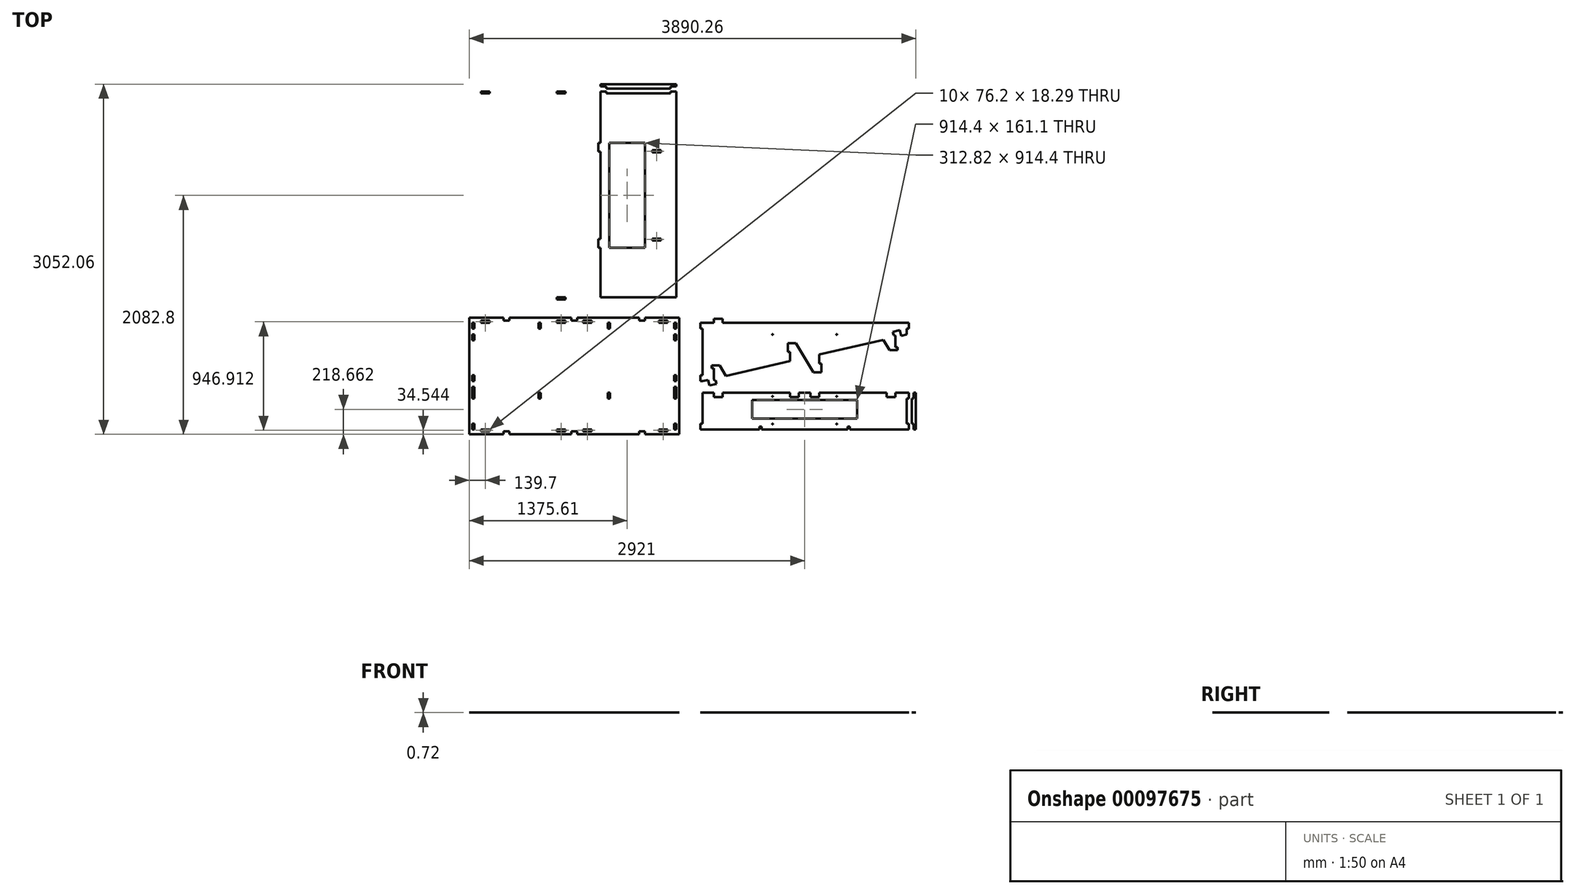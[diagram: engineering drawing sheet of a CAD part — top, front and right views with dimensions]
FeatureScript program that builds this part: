
annotation { "Feature Type Name" : "Feature", "Feature Type Description" : "" }
export const myFeature = defineFeature(function(context is Context, id is Id, definition is map)
    precondition{}
    {
        {
            assignVariable(context, id + "F0", {"name" : "ply34", "anyValue" : .72});
        }
        {
            var Q0;
            Q0=qCreatedBy(makeId("Top.planeOp"),FACE);
            var sketch = newSketch(context, id + "F1", { "sketchPlane" : qUnion([Q0])});
            skLineSegment(sketch, "E0.bottom", {"start": v(914.4, 508) * mm, "end": v(-914.4, 508) * mm});
            skLineSegment(sketch, "E0.top", {"start": v(914.4, -508) * mm, "end": v(-914.4, -508) * mm});
            skLineSegment(sketch, "E0.left", {"start": v(914.4, 508) * mm, "end": v(914.4, -508) * mm});
            skLineSegment(sketch, "E0.right", {"start": v(-914.4, 508) * mm, "end": v(-914.4, -508) * mm});
            skPoint(sketch, "E0.middle", {"position": v(0, 0) * mm});
            skLineSegment(sketch, "E1.bottom", {"start": v(889, 482.6) * mm, "end": v(-889, 482.6) * mm, "construction": true});
            skLineSegment(sketch, "E1.top", {"start": v(889, -482.6) * mm, "end": v(-889, -482.6) * mm, "construction": true});
            skLineSegment(sketch, "E1.left", {"start": v(889, 482.6) * mm, "end": v(889, -482.6) * mm, "construction": true});
            skLineSegment(sketch, "E1.right", {"start": v(-889, 482.6) * mm, "end": v(-889, -482.6) * mm, "construction": true});
            skLineSegment(sketch, "E2", {"start": v(0, 482.6) * mm, "end": v(0, -482.6) * mm, "construction": true});
            skLineSegment(sketch, "E3", {"start": v(0, 0) * mm, "end": v(-889, 0) * mm, "construction": true});
            skLineSegment(sketch, "E4", {"start": v(-444.5, 482.6) * mm, "end": v(-444.5, -482.6) * mm, "construction": true});
            skPoint(sketch, "E4.startSnap0", {"position": v(-444.5, 0) * mm});
            skLineSegment(sketch, "E5.bottom", {"start": v(-812.8, 482.6) * mm, "end": v(-736.6, 482.6) * mm});
            skLineSegment(sketch, "E5.top", {"start": v(-812.8, 464.31) * mm, "end": v(-736.6, 464.31) * mm});
            skLineSegment(sketch, "E5.left", {"start": v(-812.8, 482.6) * mm, "end": v(-812.8, 464.31) * mm});
            skLineSegment(sketch, "E5.right", {"start": v(-736.6, 482.6) * mm, "end": v(-736.6, 464.31) * mm});
            skLineSegment(sketch, "E6.MirrorCS", {"start": v(-76.2, 482.6) * mm, "end": v(-152.4, 482.6) * mm});
            skLineSegment(sketch, "E7.MirrorCS", {"start": v(-76.2, 464.31) * mm, "end": v(-152.4, 464.31) * mm});
            skLineSegment(sketch, "E8.MirrorCS", {"start": v(-152.4, 482.6) * mm, "end": v(-152.4, 464.31) * mm});
            skLineSegment(sketch, "E9.MirrorCS", {"start": v(-76.2, 482.6) * mm, "end": v(-76.2, 464.31) * mm});
            skLineSegment(sketch, "E10.MirrorCS", {"start": v(76.2, 482.6) * mm, "end": v(76.2, 464.31) * mm});
            skLineSegment(sketch, "E11.MirrorCS", {"start": v(736.6, 482.6) * mm, "end": v(736.6, 464.31) * mm});
            skLineSegment(sketch, "E12.MirrorCS", {"start": v(152.4, 482.6) * mm, "end": v(152.4, 464.31) * mm});
            skLineSegment(sketch, "E13.MirrorCS", {"start": v(812.8, 482.6) * mm, "end": v(812.8, 464.31) * mm});
            skLineSegment(sketch, "E14.MirrorCS", {"start": v(812.8, 482.6) * mm, "end": v(736.6, 482.6) * mm});
            skLineSegment(sketch, "E15.MirrorCS", {"start": v(76.2, 482.6) * mm, "end": v(152.4, 482.6) * mm});
            skLineSegment(sketch, "E16.MirrorCS", {"start": v(812.8, 464.31) * mm, "end": v(736.6, 464.31) * mm});
            skLineSegment(sketch, "E17.MirrorCS", {"start": v(76.2, 464.31) * mm, "end": v(152.4, 464.31) * mm});
            skLineSegment(sketch, "E18.MirrorCS", {"start": v(812.8, -482.6) * mm, "end": v(812.8, -464.31) * mm});
            skLineSegment(sketch, "E19.MirrorCS", {"start": v(-76.2, -482.6) * mm, "end": v(-76.2, -464.31) * mm});
            skLineSegment(sketch, "E20.MirrorCS", {"start": v(736.6, -482.6) * mm, "end": v(736.6, -464.31) * mm});
            skLineSegment(sketch, "E21.MirrorCS", {"start": v(-152.4, -482.6) * mm, "end": v(-152.4, -464.31) * mm});
            skLineSegment(sketch, "E22.MirrorCS", {"start": v(152.4, -482.6) * mm, "end": v(152.4, -464.31) * mm});
            skLineSegment(sketch, "E23.MirrorCS", {"start": v(-812.8, -482.6) * mm, "end": v(-812.8, -464.31) * mm});
            skLineSegment(sketch, "E24.MirrorCS", {"start": v(76.2, -482.6) * mm, "end": v(76.2, -464.31) * mm});
            skLineSegment(sketch, "E25.MirrorCS", {"start": v(-736.6, -482.6) * mm, "end": v(-736.6, -464.31) * mm});
            skLineSegment(sketch, "E26.MirrorCS", {"start": v(76.2, -482.6) * mm, "end": v(152.4, -482.6) * mm});
            skLineSegment(sketch, "E27.MirrorCS", {"start": v(812.8, -464.31) * mm, "end": v(736.6, -464.31) * mm});
            skLineSegment(sketch, "E28.MirrorCS", {"start": v(812.8, -482.6) * mm, "end": v(736.6, -482.6) * mm});
            skLineSegment(sketch, "E29.MirrorCS", {"start": v(-76.2, -464.31) * mm, "end": v(-152.4, -464.31) * mm});
            skLineSegment(sketch, "E30.MirrorCS", {"start": v(-76.2, -482.6) * mm, "end": v(-152.4, -482.6) * mm});
            skLineSegment(sketch, "E31.MirrorCS", {"start": v(76.2, -464.31) * mm, "end": v(152.4, -464.31) * mm});
            skLineSegment(sketch, "E32.MirrorCS", {"start": v(-812.8, -464.31) * mm, "end": v(-736.6, -464.31) * mm});
            skLineSegment(sketch, "E33.MirrorCS", {"start": v(-812.8, -482.6) * mm, "end": v(-736.6, -482.6) * mm});
            skLineSegment(sketch, "E34.bottom", {"start": v(292.1, 464.31) * mm, "end": v(310.39, 464.31) * mm});
            skLineSegment(sketch, "E34.top", {"start": v(292.1, 413.51) * mm, "end": v(310.39, 413.51) * mm});
            skLineSegment(sketch, "E34.left", {"start": v(292.1, 464.31) * mm, "end": v(292.1, 413.51) * mm});
            skLineSegment(sketch, "E34.right", {"start": v(310.39, 464.31) * mm, "end": v(310.39, 413.51) * mm});
            skLineSegment(sketch, "E35.bottom", {"start": v(292.1, -145.29) * mm, "end": v(310.39, -145.29) * mm});
            skLineSegment(sketch, "E35.top", {"start": v(292.1, -196.09) * mm, "end": v(310.39, -196.09) * mm});
            skLineSegment(sketch, "E35.left", {"start": v(292.1, -145.29) * mm, "end": v(292.1, -196.09) * mm});
            skLineSegment(sketch, "E35.right", {"start": v(310.39, -145.29) * mm, "end": v(310.39, -196.09) * mm});
            skLineSegment(sketch, "E36.MirrorCS", {"start": v(-292.1, -196.09) * mm, "end": v(-310.39, -196.09) * mm});
            skLineSegment(sketch, "E37.MirrorCS", {"start": v(-292.1, -145.29) * mm, "end": v(-310.39, -145.29) * mm});
            skLineSegment(sketch, "E38.MirrorCS", {"start": v(-292.1, 413.51) * mm, "end": v(-310.39, 413.51) * mm});
            skLineSegment(sketch, "E39.MirrorCS", {"start": v(-292.1, 464.31) * mm, "end": v(-310.39, 464.31) * mm});
            skLineSegment(sketch, "E40.MirrorCS", {"start": v(-292.1, -145.29) * mm, "end": v(-292.1, -196.09) * mm});
            skLineSegment(sketch, "E41.MirrorCS", {"start": v(-310.39, 464.31) * mm, "end": v(-310.39, 413.51) * mm});
            skLineSegment(sketch, "E42.MirrorCS", {"start": v(-310.39, -145.29) * mm, "end": v(-310.39, -196.09) * mm});
            skLineSegment(sketch, "E43.MirrorCS", {"start": v(-292.1, 464.31) * mm, "end": v(-292.1, 413.51) * mm});
            skLineSegment(sketch, "E44.bottom", {"start": v(-889, 685.8) * mm, "end": v(0, 685.8) * mm});
            skLineSegment(sketch, "E44.top", {"start": v(-889, 2463.8) * mm, "end": v(0, 2463.8) * mm});
            skLineSegment(sketch, "E44.left", {"start": v(-889, 685.8) * mm, "end": v(-889, 2463.8) * mm});
            skLineSegment(sketch, "E44.right", {"start": v(0, 685.8) * mm, "end": v(0, 2463.8) * mm});
            skLineSegment(sketch, "E45.bottom", {"start": v(-812.8, 685.8) * mm, "end": v(-736.6, 685.8) * mm});
            skLineSegment(sketch, "E45.top", {"start": v(-812.8, 667.51) * mm, "end": v(-736.6, 667.51) * mm});
            skLineSegment(sketch, "E45.left", {"start": v(-812.8, 685.8) * mm, "end": v(-812.8, 667.51) * mm});
            skLineSegment(sketch, "E45.right", {"start": v(-736.6, 685.8) * mm, "end": v(-736.6, 667.51) * mm});
            skLineSegment(sketch, "E46", {"start": v(-444.5, 685.8) * mm, "end": v(-444.5, 2463.8) * mm, "construction": true});
            skLineSegment(sketch, "E47", {"start": v(0, 1574.8) * mm, "end": v(-889, 1574.8) * mm, "construction": true});
            skLineSegment(sketch, "E48.MirrorCS", {"start": v(-76.2, 667.51) * mm, "end": v(-152.4, 667.51) * mm});
            skLineSegment(sketch, "E49.MirrorCS", {"start": v(-76.2, 685.8) * mm, "end": v(-152.4, 685.8) * mm});
            skLineSegment(sketch, "E50.MirrorCS", {"start": v(-152.4, 685.8) * mm, "end": v(-152.4, 667.51) * mm});
            skLineSegment(sketch, "E51.MirrorCS", {"start": v(-76.2, 685.8) * mm, "end": v(-76.2, 667.51) * mm});
            skLineSegment(sketch, "E52.MirrorCS", {"start": v(-812.8, 2482.09) * mm, "end": v(-736.6, 2482.09) * mm});
            skLineSegment(sketch, "E53.MirrorCS", {"start": v(-812.8, 2463.8) * mm, "end": v(-736.6, 2463.8) * mm});
            skLineSegment(sketch, "E54.MirrorCS", {"start": v(-812.8, 2463.8) * mm, "end": v(-812.8, 2482.09) * mm});
            skLineSegment(sketch, "E55.MirrorCS", {"start": v(-736.6, 2463.8) * mm, "end": v(-736.6, 2482.09) * mm});
            skLineSegment(sketch, "E56.MirrorCS", {"start": v(-152.4, 2463.8) * mm, "end": v(-152.4, 2482.09) * mm});
            skLineSegment(sketch, "E57.MirrorCS", {"start": v(-76.2, 2463.8) * mm, "end": v(-76.2, 2482.09) * mm});
            skLineSegment(sketch, "E58.MirrorCS", {"start": v(-76.2, 2482.09) * mm, "end": v(-152.4, 2482.09) * mm});
            skLineSegment(sketch, "E59.MirrorCS", {"start": v(-76.2, 2463.8) * mm, "end": v(-152.4, 2463.8) * mm});
            skLineSegment(sketch, "E60.0", {"start": v(870.71, 464.31) * mm, "end": v(-870.71, 464.31) * mm, "construction": true});
            skLineSegment(sketch, "E60.1", {"start": v(870.71, 464.31) * mm, "end": v(870.71, -464.31) * mm, "construction": true});
            skLineSegment(sketch, "E60.2", {"start": v(870.71, -464.31) * mm, "end": v(-870.71, -464.31) * mm, "construction": true});
            skLineSegment(sketch, "E60.3", {"start": v(-870.71, 464.31) * mm, "end": v(-870.71, -464.31) * mm, "construction": true});
            skLineSegment(sketch, "E61.bottom", {"start": v(-310.39, 464.31) * mm, "end": v(-292.1, 464.31) * mm, "construction": true});
            skLineSegment(sketch, "E61.top", {"start": v(-310.39, -196.09) * mm, "end": v(-292.1, -196.09) * mm, "construction": true});
            skLineSegment(sketch, "E61.left", {"start": v(-310.39, 464.31) * mm, "end": v(-310.39, -196.09) * mm, "construction": true});
            skLineSegment(sketch, "E61.right", {"start": v(-292.1, 464.31) * mm, "end": v(-292.1, -196.09) * mm, "construction": true});
            skLineSegment(sketch, "E62.bottom", {"start": v(292.1, 464.31) * mm, "end": v(310.39, 464.31) * mm, "construction": true});
            skLineSegment(sketch, "E62.top", {"start": v(292.1, -196.09) * mm, "end": v(310.39, -196.09) * mm, "construction": true});
            skLineSegment(sketch, "E62.left", {"start": v(292.1, 464.31) * mm, "end": v(292.1, -196.09) * mm, "construction": true});
            skLineSegment(sketch, "E62.right", {"start": v(310.39, 464.31) * mm, "end": v(310.39, -196.09) * mm, "construction": true});
            skLineSegment(sketch, "E63.bottom", {"start": v(228.6, 685.8) * mm, "end": v(889, 685.8) * mm});
            skLineSegment(sketch, "E63.top", {"start": v(228.6, 2463.8) * mm, "end": v(889, 2463.8) * mm});
            skLineSegment(sketch, "E63.left", {"start": v(228.6, 685.8) * mm, "end": v(228.6, 2463.8) * mm});
            skLineSegment(sketch, "E63.right", {"start": v(889, 685.8) * mm, "end": v(889, 2463.8) * mm});
            skLineSegment(sketch, "E64.bottom", {"start": v(228.6, 685.8) * mm, "end": v(279.4, 685.8) * mm});
            skLineSegment(sketch, "E64.top", {"start": v(228.6, 667.51) * mm, "end": v(279.4, 667.51) * mm});
            skLineSegment(sketch, "E64.left", {"start": v(228.6, 685.8) * mm, "end": v(228.6, 667.51) * mm});
            skLineSegment(sketch, "E64.right", {"start": v(279.4, 685.8) * mm, "end": v(279.4, 667.51) * mm});
            skLineSegment(sketch, "E65", {"start": v(558.8, 685.8) * mm, "end": v(558.8, 2463.8) * mm, "construction": true});
            skLineSegment(sketch, "E66", {"start": v(889, 1574.8) * mm, "end": v(228.6, 1574.8) * mm, "construction": true});
            skLineSegment(sketch, "E67.MirrorCS", {"start": v(889, 685.8) * mm, "end": v(838.2, 685.8) * mm});
            skLineSegment(sketch, "E68.MirrorCS", {"start": v(838.2, 685.8) * mm, "end": v(838.2, 667.51) * mm});
            skLineSegment(sketch, "E69.MirrorCS", {"start": v(889, 667.51) * mm, "end": v(838.2, 667.51) * mm});
            skLineSegment(sketch, "E70.MirrorCS", {"start": v(889, 685.8) * mm, "end": v(889, 667.51) * mm});
            skLineSegment(sketch, "E71.MirrorCS", {"start": v(889, 2463.8) * mm, "end": v(889, 2482.09) * mm});
            skLineSegment(sketch, "E72.MirrorCS", {"start": v(889, 2482.09) * mm, "end": v(838.2, 2482.09) * mm});
            skLineSegment(sketch, "E73.MirrorCS", {"start": v(838.2, 2463.8) * mm, "end": v(838.2, 2482.09) * mm});
            skLineSegment(sketch, "E74.MirrorCS", {"start": v(889, 2463.8) * mm, "end": v(838.2, 2463.8) * mm});
            skLineSegment(sketch, "E75.MirrorCS", {"start": v(228.6, 2463.8) * mm, "end": v(228.6, 2482.09) * mm});
            skLineSegment(sketch, "E76.MirrorCS", {"start": v(228.6, 2463.8) * mm, "end": v(279.4, 2463.8) * mm});
            skLineSegment(sketch, "E77.MirrorCS", {"start": v(279.4, 2463.8) * mm, "end": v(279.4, 2482.09) * mm});
            skLineSegment(sketch, "E78.MirrorCS", {"start": v(228.6, 2482.09) * mm, "end": v(279.4, 2482.09) * mm});
            skPoint(sketch, "E79.middle", {"position": v(558.8, 1574.8) * mm});
            skLineSegment(sketch, "E80.bottom", {"start": v(304.8, 2032) * mm, "end": v(617.62, 2032) * mm});
            skLineSegment(sketch, "E80.top", {"start": v(304.8, 1117.6) * mm, "end": v(617.62, 1117.6) * mm});
            skLineSegment(sketch, "E80.left", {"start": v(304.8, 2032) * mm, "end": v(304.8, 1117.6) * mm});
            skLineSegment(sketch, "E80.right", {"start": v(617.62, 2032) * mm, "end": v(617.62, 1117.6) * mm});
            skLineSegment(sketch, "E81", {"start": v(304.8, 1574.8) * mm, "end": v(617.62, 1574.8) * mm});
            skLineSegment(sketch, "E82.bottom", {"start": v(1117.6, 464.31) * mm, "end": v(2895.6, 464.31) * mm, "construction": true});
            skLineSegment(sketch, "E82.top", {"start": v(1117.6, -145.29) * mm, "end": v(2895.6, -145.29) * mm, "construction": true});
            skLineSegment(sketch, "E82.left", {"start": v(1117.6, 464.31) * mm, "end": v(1117.6, -145.29) * mm, "construction": true});
            skLineSegment(sketch, "E82.right", {"start": v(2895.6, 464.31) * mm, "end": v(2895.6, -145.29) * mm, "construction": true});
            skLineSegment(sketch, "E83", {"start": v(2133.6, 464.31) * mm, "end": v(2133.6, -145.29) * mm, "construction": true});
            skLineSegment(sketch, "E84", {"start": v(1117.6, -43.69) * mm, "end": v(2895.6, -43.69) * mm, "construction": true});
            skLineSegment(sketch, "E85", {"start": v(1117.6, 362.71) * mm, "end": v(2895.6, 362.71) * mm, "construction": true});
            skLineSegment(sketch, "E86", {"start": v(1117.6, 464.31) * mm, "end": v(2895.6, 464.31) * mm});
            skLineSegment(sketch, "E87", {"start": v(2895.6, 464.31) * mm, "end": v(2895.6, 362.71) * mm});
            skLineSegment(sketch, "E88", {"start": v(2895.6, 362.71) * mm, "end": v(1117.6, -43.69) * mm});
            skLineSegment(sketch, "E89", {"start": v(1117.6, -43.69) * mm, "end": v(1117.6, 464.31) * mm});
            skLineSegment(sketch, "E90", {"start": v(2133.6, 188.54) * mm, "end": v(2133.6, 32.51) * mm});
            skLineSegment(sketch, "E91", {"start": v(2133.6, 32.51) * mm, "end": v(2082.8, 32.51) * mm});
            skLineSegment(sketch, "E92", {"start": v(2082.8, 32.51) * mm, "end": v(2006.6, 159.51) * mm});
            skLineSegment(sketch, "E93.bottom", {"start": v(2133.6, 464.31) * mm, "end": v(2057.4, 464.31) * mm});
            skLineSegment(sketch, "E93.top", {"start": v(2133.6, 500.89) * mm, "end": v(2057.4, 500.89) * mm});
            skLineSegment(sketch, "E93.left", {"start": v(2133.6, 464.31) * mm, "end": v(2133.6, 500.89) * mm});
            skLineSegment(sketch, "E93.right", {"start": v(2057.4, 464.31) * mm, "end": v(2057.4, 500.89) * mm});
            skLineSegment(sketch, "E94.bottom", {"start": v(2133.6, 32.51) * mm, "end": v(2151.89, 32.51) * mm});
            skLineSegment(sketch, "E94.top", {"start": v(2133.6, 108.71) * mm, "end": v(2151.89, 108.71) * mm});
            skLineSegment(sketch, "E94.left", {"start": v(2133.6, 32.51) * mm, "end": v(2133.6, 108.71) * mm});
            skLineSegment(sketch, "E94.right", {"start": v(2151.89, 32.51) * mm, "end": v(2151.89, 108.71) * mm});
            skLineSegment(sketch, "E95", {"start": v(1879.6, 464.31) * mm, "end": v(1879.6, -145.29) * mm, "construction": true});
            skLineSegment(sketch, "E96.bottom", {"start": v(1879.6, 286.51) * mm, "end": v(1861.31, 286.51) * mm});
            skLineSegment(sketch, "E96.top", {"start": v(1879.6, 210.31) * mm, "end": v(1861.31, 210.31) * mm});
            skLineSegment(sketch, "E96.left", {"start": v(1879.6, 286.51) * mm, "end": v(1879.6, 210.31) * mm});
            skLineSegment(sketch, "E96.right", {"start": v(1861.31, 286.51) * mm, "end": v(1861.31, 210.31) * mm});
            skLineSegment(sketch, "E97", {"start": v(1879.6, 286.51) * mm, "end": v(1930.4, 286.51) * mm});
            skLineSegment(sketch, "E98", {"start": v(1879.6, 210.31) * mm, "end": v(1879.6, 130.48) * mm});
            skLineSegment(sketch, "E99.bottom", {"start": v(1879.6, -145.29) * mm, "end": v(1955.8, -145.29) * mm});
            skLineSegment(sketch, "E99.top", {"start": v(1879.6, -181.86) * mm, "end": v(1955.8, -181.86) * mm});
            skLineSegment(sketch, "E99.left", {"start": v(1879.6, -145.29) * mm, "end": v(1879.6, -181.86) * mm});
            skLineSegment(sketch, "E99.right", {"start": v(1955.8, -145.29) * mm, "end": v(1955.8, -181.86) * mm});
            skLineSegment(sketch, "E100", {"start": v(1117.6, -43.69) * mm, "end": v(1117.6, -145.29) * mm});
            skLineSegment(sketch, "E101", {"start": v(2895.6, -145.29) * mm, "end": v(1117.6, -145.29) * mm});
            skLineSegment(sketch, "E102", {"start": v(2895.6, -145.29) * mm, "end": v(2895.6, 362.71) * mm});
            skLineSegment(sketch, "E103", {"start": v(2006.6, 159.51) * mm, "end": v(1930.4, 286.51) * mm});
            skLineSegment(sketch, "E104.0", {"start": v(678.69, 2032) * mm, "end": v(678.69, 1117.6) * mm, "construction": true});
            skLineSegment(sketch, "E105.bottom", {"start": v(678.69, 1181.1) * mm, "end": v(754.89, 1181.1) * mm});
            skLineSegment(sketch, "E105.top", {"start": v(678.69, 1199.39) * mm, "end": v(754.89, 1199.39) * mm});
            skLineSegment(sketch, "E105.left", {"start": v(678.69, 1181.1) * mm, "end": v(678.69, 1199.39) * mm});
            skLineSegment(sketch, "E105.right", {"start": v(754.89, 1181.1) * mm, "end": v(754.89, 1199.39) * mm});
            skLineSegment(sketch, "E106.MirrorCS", {"start": v(754.89, 1968.5) * mm, "end": v(754.89, 1950.21) * mm});
            skLineSegment(sketch, "E107.MirrorCS", {"start": v(678.69, 1950.21) * mm, "end": v(754.89, 1950.21) * mm});
            skLineSegment(sketch, "E108.MirrorCS", {"start": v(678.69, 1968.5) * mm, "end": v(754.89, 1968.5) * mm});
            skLineSegment(sketch, "E109.MirrorCS", {"start": v(678.69, 1968.5) * mm, "end": v(678.69, 1950.21) * mm});
            skLineSegment(sketch, "E110.bottom", {"start": v(1117.6, 464.31) * mm, "end": v(1099.31, 464.31) * mm});
            skLineSegment(sketch, "E110.top", {"start": v(1117.6, 413.51) * mm, "end": v(1099.31, 413.51) * mm});
            skLineSegment(sketch, "E110.left", {"start": v(1117.6, 464.31) * mm, "end": v(1117.6, 413.51) * mm});
            skLineSegment(sketch, "E110.right", {"start": v(1099.31, 464.31) * mm, "end": v(1099.31, 413.51) * mm});
            skLineSegment(sketch, "E111.bottom", {"start": v(1117.6, -43.69) * mm, "end": v(1099.31, -43.69) * mm});
            skLineSegment(sketch, "E111.top", {"start": v(1117.6, 7.11) * mm, "end": v(1099.31, 7.11) * mm});
            skLineSegment(sketch, "E111.left", {"start": v(1117.6, -43.69) * mm, "end": v(1117.6, 7.11) * mm});
            skLineSegment(sketch, "E111.right", {"start": v(1099.31, -43.69) * mm, "end": v(1099.31, 7.11) * mm});
            skLineSegment(sketch, "E112.bottom", {"start": v(889, 464.31) * mm, "end": v(870.71, 464.31) * mm});
            skLineSegment(sketch, "E112.top", {"start": v(889, 413.51) * mm, "end": v(870.71, 413.51) * mm});
            skLineSegment(sketch, "E112.left", {"start": v(889, 464.31) * mm, "end": v(889, 413.51) * mm});
            skLineSegment(sketch, "E112.right", {"start": v(870.71, 464.31) * mm, "end": v(870.71, 413.51) * mm});
            skLineSegment(sketch, "E113.bottom", {"start": v(1099.31, -94.49) * mm, "end": v(1117.6, -94.49) * mm});
            skLineSegment(sketch, "E113.top", {"start": v(1099.31, -145.29) * mm, "end": v(1117.6, -145.29) * mm});
            skLineSegment(sketch, "E113.left", {"start": v(1099.31, -94.49) * mm, "end": v(1099.31, -145.29) * mm});
            skLineSegment(sketch, "E113.right", {"start": v(1117.6, -94.49) * mm, "end": v(1117.6, -145.29) * mm});
            skLineSegment(sketch, "E114.bottom", {"start": v(889, -94.49) * mm, "end": v(870.71, -94.49) * mm});
            skLineSegment(sketch, "E114.top", {"start": v(889, -145.29) * mm, "end": v(870.71, -145.29) * mm});
            skLineSegment(sketch, "E114.left", {"start": v(889, -94.49) * mm, "end": v(889, -145.29) * mm});
            skLineSegment(sketch, "E114.right", {"start": v(870.71, -94.49) * mm, "end": v(870.71, -145.29) * mm});
            skLineSegment(sketch, "E115.MirrorCS", {"start": v(-889, 464.31) * mm, "end": v(-870.71, 464.31) * mm});
            skLineSegment(sketch, "E116.MirrorCS", {"start": v(-889, -145.29) * mm, "end": v(-870.71, -145.29) * mm});
            skLineSegment(sketch, "E117.MirrorCS", {"start": v(-889, -94.49) * mm, "end": v(-870.71, -94.49) * mm});
            skLineSegment(sketch, "E118.MirrorCS", {"start": v(-889, 413.51) * mm, "end": v(-870.71, 413.51) * mm});
            skLineSegment(sketch, "E119.MirrorCS", {"start": v(-870.71, -94.49) * mm, "end": v(-870.71, -145.29) * mm});
            skLineSegment(sketch, "E120.MirrorCS", {"start": v(-889, -94.49) * mm, "end": v(-889, -145.29) * mm});
            skLineSegment(sketch, "E121.MirrorCS", {"start": v(-870.71, 464.31) * mm, "end": v(-870.71, 413.51) * mm});
            skLineSegment(sketch, "E122.MirrorCS", {"start": v(-889, 464.31) * mm, "end": v(-889, 413.51) * mm});
            skLineSegment(sketch, "E123", {"start": v(-50.8, 2463.8) * mm, "end": v(-50.8, 685.8) * mm, "construction": true});
            skLineSegment(sketch, "E124.bottom", {"start": v(889, 7.11) * mm, "end": v(870.71, 7.11) * mm});
            skLineSegment(sketch, "E124.top", {"start": v(889, -43.69) * mm, "end": v(870.71, -43.69) * mm});
            skLineSegment(sketch, "E124.left", {"start": v(889, 7.11) * mm, "end": v(889, -43.69) * mm});
            skLineSegment(sketch, "E124.right", {"start": v(870.71, 7.11) * mm, "end": v(870.71, -43.69) * mm});
            skLineSegment(sketch, "E125.MirrorCS", {"start": v(-870.71, 7.11) * mm, "end": v(-870.71, -43.69) * mm});
            skLineSegment(sketch, "E126.MirrorCS", {"start": v(-889, 7.11) * mm, "end": v(-889, -43.69) * mm});
            skLineSegment(sketch, "E127.MirrorCS", {"start": v(-889, -43.69) * mm, "end": v(-870.71, -43.69) * mm});
            skLineSegment(sketch, "E128.MirrorCS", {"start": v(-889, 7.11) * mm, "end": v(-870.71, 7.11) * mm});
            skLineSegment(sketch, "E129.MirrorCS", {"start": v(-838.2, 2463.8) * mm, "end": v(-838.2, 685.8) * mm, "construction": true});
            skLineSegment(sketch, "E130.0", {"start": v(1117.6, 482.6) * mm, "end": v(2895.6, 482.6) * mm, "construction": true});
            skLineSegment(sketch, "E131", {"start": v(1203.45, -24.06) * mm, "end": v(2936.75, 372.12) * mm, "construction": true});
            skLineSegment(sketch, "E132", {"start": v(2936.75, 372.12) * mm, "end": v(2940.82, 354.29) * mm, "construction": true});
            skLineSegment(sketch, "E133", {"start": v(2940.82, 354.29) * mm, "end": v(1207.53, -41.9) * mm, "construction": true});
            skLineSegment(sketch, "E134", {"start": v(1207.53, -41.9) * mm, "end": v(1203.45, -24.06) * mm, "construction": true});
            skLineSegment(sketch, "E135", {"start": v(2006.6, 159.51) * mm, "end": v(2133.6, 188.54) * mm, "construction": true});
            skPoint(sketch, "E136", {"position": v(2070.1, 174.03) * mm});
            skLineSegment(sketch, "E137.bottom", {"start": v(-50.8, 1676.4) * mm, "end": v(-69.09, 1676.4) * mm});
            skLineSegment(sketch, "E137.top", {"start": v(-50.8, 1473.2) * mm, "end": v(-69.09, 1473.2) * mm});
            skLineSegment(sketch, "E137.left", {"start": v(-50.8, 1676.4) * mm, "end": v(-50.8, 1473.2) * mm});
            skLineSegment(sketch, "E137.right", {"start": v(-69.09, 1676.4) * mm, "end": v(-69.09, 1473.2) * mm});
            skPoint(sketch, "E137.middle", {"position": v(-59.94, 1574.8) * mm});
            skLineSegment(sketch, "E138.bottom", {"start": v(-838.2, 685.8) * mm, "end": v(-819.91, 685.8) * mm});
            skLineSegment(sketch, "E138.top", {"start": v(-838.2, 698.5) * mm, "end": v(-819.91, 698.5) * mm});
            skLineSegment(sketch, "E138.left", {"start": v(-838.2, 685.8) * mm, "end": v(-838.2, 698.5) * mm});
            skLineSegment(sketch, "E138.right", {"start": v(-819.91, 685.8) * mm, "end": v(-819.91, 698.5) * mm});
            skLineSegment(sketch, "E139.MirrorCS", {"start": v(-69.09, 685.8) * mm, "end": v(-69.09, 698.5) * mm});
            skLineSegment(sketch, "E140.MirrorCS", {"start": v(-50.8, 685.8) * mm, "end": v(-50.8, 698.5) * mm});
            skLineSegment(sketch, "E141.MirrorCS", {"start": v(-50.8, 685.8) * mm, "end": v(-69.09, 685.8) * mm});
            skLineSegment(sketch, "E142.MirrorCS", {"start": v(-50.8, 698.5) * mm, "end": v(-69.09, 698.5) * mm});
            skLineSegment(sketch, "E143.MirrorCS", {"start": v(-69.09, 2463.8) * mm, "end": v(-69.09, 2451.1) * mm});
            skLineSegment(sketch, "E144.MirrorCS", {"start": v(-50.8, 2463.8) * mm, "end": v(-50.8, 2451.1) * mm});
            skLineSegment(sketch, "E145.MirrorCS", {"start": v(-50.8, 2463.8) * mm, "end": v(-69.09, 2463.8) * mm});
            skLineSegment(sketch, "E146.MirrorCS", {"start": v(-50.8, 2451.1) * mm, "end": v(-69.09, 2451.1) * mm});
            skLineSegment(sketch, "E147.MirrorCS", {"start": v(-838.2, 2463.8) * mm, "end": v(-819.91, 2463.8) * mm});
            skLineSegment(sketch, "E148.MirrorCS", {"start": v(-838.2, 2451.1) * mm, "end": v(-819.91, 2451.1) * mm});
            skLineSegment(sketch, "E149.MirrorCS", {"start": v(-819.91, 2463.8) * mm, "end": v(-819.91, 2451.1) * mm});
            skLineSegment(sketch, "E150.MirrorCS", {"start": v(-838.2, 2463.8) * mm, "end": v(-838.2, 2451.1) * mm});
            skLineSegment(sketch, "E151", {"start": v(1219.9, -39.06) * mm, "end": v(1215.83, -21.24) * mm});
            skLineSegment(sketch, "E152", {"start": v(1219.9, -39.06) * mm, "end": v(1232.29, -36.23) * mm});
            skLineSegment(sketch, "E153", {"start": v(1232.29, -36.23) * mm, "end": v(1239.36, -67.19) * mm});
            skLineSegment(sketch, "E154", {"start": v(1239.36, -67.19) * mm, "end": v(1177.46, -81.33) * mm});
            skLineSegment(sketch, "E155", {"start": v(1177.46, -81.33) * mm, "end": v(1166.3, -32.55) * mm});
            skLineSegment(sketch, "E156", {"start": v(1215.83, -21.24) * mm, "end": v(1215.83, 91.95) * mm});
            skLineSegment(sketch, "E157", {"start": v(1215.83, 91.95) * mm, "end": v(1266.63, 91.95) * mm});
            skLineSegment(sketch, "E158", {"start": v(1266.63, 91.95) * mm, "end": v(1320.22, 2.63) * mm});
            skLineSegment(sketch, "E159.bottom", {"start": v(1215.83, 91.95) * mm, "end": v(1197.54, 91.95) * mm});
            skLineSegment(sketch, "E159.top", {"start": v(1215.83, 66.55) * mm, "end": v(1197.54, 66.55) * mm});
            skLineSegment(sketch, "E159.left", {"start": v(1215.83, 91.95) * mm, "end": v(1215.83, 66.55) * mm});
            skLineSegment(sketch, "E159.right", {"start": v(1197.54, 91.95) * mm, "end": v(1197.54, 66.55) * mm});
            skLineSegment(sketch, "E160", {"start": v(2006.6, 159.51) * mm, "end": v(2066.03, -100.5) * mm, "construction": true});
            skLineSegment(sketch, "E161.MirrorCS", {"start": v(2801.44, 322.43) * mm, "end": v(2789.06, 319.6) * mm, "construction": true});
            skLineSegment(sketch, "E162.MirrorCS", {"start": v(2789.06, 319.6) * mm, "end": v(2796.14, 288.65) * mm, "construction": true});
            skLineSegment(sketch, "E163.MirrorCS", {"start": v(2813.82, 325.26) * mm, "end": v(2809.75, 343.09) * mm, "construction": true});
            skLineSegment(sketch, "E164.MirrorCS", {"start": v(2801.44, 322.43) * mm, "end": v(2797.37, 340.26) * mm, "construction": true});
            skLineSegment(sketch, "E165.MirrorCS", {"start": v(2748.2, 442.2) * mm, "end": v(2764.67, 450.15) * mm, "construction": true});
            skLineSegment(sketch, "E166.MirrorCS", {"start": v(2759.23, 419.33) * mm, "end": v(2775.7, 427.27) * mm, "construction": true});
            skLineSegment(sketch, "E167.MirrorCS", {"start": v(2796.14, 288.65) * mm, "end": v(2858.04, 302.8) * mm, "construction": true});
            skLineSegment(sketch, "E168.MirrorCS", {"start": v(2797.37, 340.26) * mm, "end": v(2748.2, 442.2) * mm, "construction": true});
            skLineSegment(sketch, "E169.MirrorCS", {"start": v(2858.04, 302.8) * mm, "end": v(2846.9, 351.58) * mm, "construction": true});
            skLineSegment(sketch, "E170.MirrorCS", {"start": v(2748.2, 442.2) * mm, "end": v(2702.44, 420.13) * mm, "construction": true});
            skLineSegment(sketch, "E171.MirrorCS", {"start": v(2702.44, 420.13) * mm, "end": v(2692.98, 316.4) * mm, "construction": true});
            skLineSegment(sketch, "E172.MirrorCS", {"start": v(2748.2, 442.2) * mm, "end": v(2759.23, 419.33) * mm, "construction": true});
            skLineSegment(sketch, "E173.MirrorCS", {"start": v(2764.67, 450.15) * mm, "end": v(2775.7, 427.27) * mm, "construction": true});
            skLineSegment(sketch, "E174.MirrorCS", {"start": v(2797.37, 252.48) * mm, "end": v(2815.66, 252.48) * mm});
            skLineSegment(sketch, "E175.MirrorCS", {"start": v(2793.3, 358.09) * mm, "end": v(2780.91, 355.26) * mm});
            skLineSegment(sketch, "E176.MirrorCS", {"start": v(2797.37, 227.08) * mm, "end": v(2815.66, 227.08) * mm});
            skLineSegment(sketch, "E177.MirrorCS", {"start": v(2793.3, 358.09) * mm, "end": v(2797.37, 340.26) * mm});
            skLineSegment(sketch, "E178.MirrorCS", {"start": v(2805.67, 360.92) * mm, "end": v(2809.75, 343.09) * mm, "construction": true});
            skLineSegment(sketch, "E179.MirrorCS", {"start": v(2797.37, 340.26) * mm, "end": v(2797.37, 227.08) * mm});
            skLineSegment(sketch, "E180.MirrorCS", {"start": v(2773.84, 386.2) * mm, "end": v(2835.74, 400.36) * mm});
            skLineSegment(sketch, "E181.MirrorCS", {"start": v(2780.91, 355.26) * mm, "end": v(2773.84, 386.2) * mm});
            skLineSegment(sketch, "E182.MirrorCS", {"start": v(2815.66, 227.08) * mm, "end": v(2815.66, 252.48) * mm});
            skLineSegment(sketch, "E183.MirrorCS", {"start": v(2797.37, 227.08) * mm, "end": v(2797.37, 252.48) * mm});
            skLineSegment(sketch, "E184.MirrorCS", {"start": v(2746.57, 227.08) * mm, "end": v(2692.98, 316.4) * mm});
            skLineSegment(sketch, "E185.MirrorCS", {"start": v(2797.37, 227.08) * mm, "end": v(2746.57, 227.08) * mm});
            skLineSegment(sketch, "E186.MirrorCS", {"start": v(2835.74, 400.36) * mm, "end": v(2846.9, 351.58) * mm});
            skLineSegment(sketch, "E187.bottom", {"start": v(1215.83, -145.29) * mm, "end": v(1292.03, -145.29) * mm});
            skLineSegment(sketch, "E187.top", {"start": v(1215.83, -181.86) * mm, "end": v(1292.03, -181.86) * mm});
            skLineSegment(sketch, "E187.left", {"start": v(1215.83, -145.29) * mm, "end": v(1215.83, -181.86) * mm});
            skLineSegment(sketch, "E187.right", {"start": v(1292.03, -145.29) * mm, "end": v(1292.03, -181.86) * mm});
            skLineSegment(sketch, "E188.bottom", {"start": v(2895.6, 464.31) * mm, "end": v(2913.89, 464.31) * mm});
            skLineSegment(sketch, "E188.top", {"start": v(2895.6, 413.51) * mm, "end": v(2913.89, 413.51) * mm});
            skLineSegment(sketch, "E188.left", {"start": v(2895.6, 464.31) * mm, "end": v(2895.6, 413.51) * mm});
            skLineSegment(sketch, "E188.right", {"start": v(2913.89, 464.31) * mm, "end": v(2913.89, 413.51) * mm});
            skLineSegment(sketch, "E189.bottom", {"start": v(2797.37, 464.31) * mm, "end": v(2721.17, 464.31) * mm});
            skLineSegment(sketch, "E189.top", {"start": v(2797.37, 500.89) * mm, "end": v(2721.17, 500.89) * mm});
            skLineSegment(sketch, "E189.left", {"start": v(2797.37, 464.31) * mm, "end": v(2797.37, 500.89) * mm});
            skLineSegment(sketch, "E189.right", {"start": v(2721.17, 464.31) * mm, "end": v(2721.17, 500.89) * mm});
            skLineSegment(sketch, "E190.bottom", {"start": v(2895.6, 362.71) * mm, "end": v(2913.89, 362.71) * mm});
            skLineSegment(sketch, "E190.top", {"start": v(2895.6, 311.91) * mm, "end": v(2913.89, 311.91) * mm});
            skLineSegment(sketch, "E190.left", {"start": v(2895.6, 362.71) * mm, "end": v(2895.6, 311.91) * mm});
            skLineSegment(sketch, "E190.right", {"start": v(2913.89, 362.71) * mm, "end": v(2913.89, 311.91) * mm});
            skLineSegment(sketch, "E191.bottom", {"start": v(2895.6, -145.29) * mm, "end": v(2913.89, -145.29) * mm});
            skLineSegment(sketch, "E191.top", {"start": v(2895.6, -94.49) * mm, "end": v(2913.89, -94.49) * mm});
            skLineSegment(sketch, "E191.left", {"start": v(2895.6, -145.29) * mm, "end": v(2895.6, -94.49) * mm});
            skLineSegment(sketch, "E191.right", {"start": v(2913.89, -145.29) * mm, "end": v(2913.89, -94.49) * mm});
            skLineSegment(sketch, "E192", {"start": v(2006.6, 159.51) * mm, "end": v(2006.6, -208.79) * mm, "construction": true});
            skPoint(sketch, "E192.endSnap0", {"position": v(2006.6, -145.29) * mm});
            skLineSegment(sketch, "E193.MirrorCS", {"start": v(2057.4, -145.29) * mm, "end": v(2057.4, -181.86) * mm});
            skLineSegment(sketch, "E194.MirrorCS", {"start": v(2133.6, -145.29) * mm, "end": v(2133.6, -181.86) * mm});
            skLineSegment(sketch, "E195.MirrorCS", {"start": v(2721.17, -145.29) * mm, "end": v(2721.17, -181.86) * mm});
            skLineSegment(sketch, "E196.MirrorCS", {"start": v(2797.37, -145.29) * mm, "end": v(2797.37, -181.86) * mm});
            skLineSegment(sketch, "E197.MirrorCS", {"start": v(2133.6, -181.86) * mm, "end": v(2057.4, -181.86) * mm});
            skLineSegment(sketch, "E198.MirrorCS", {"start": v(2133.6, -145.29) * mm, "end": v(2057.4, -145.29) * mm});
            skLineSegment(sketch, "E199.MirrorCS", {"start": v(2797.37, -181.86) * mm, "end": v(2721.17, -181.86) * mm});
            skLineSegment(sketch, "E200.MirrorCS", {"start": v(2797.37, -145.29) * mm, "end": v(2721.17, -145.29) * mm});
            skLineSegment(sketch, "E201", {"start": v(2692.98, 316.4) * mm, "end": v(2797.37, 340.26) * mm, "construction": true});
            skPoint(sketch, "E202", {"position": v(2745.17, 328.33) * mm});
            skLineSegment(sketch, "E203", {"start": v(-889, 2270.7) * mm, "end": v(0, 2270.7) * mm, "construction": true});
            skLineSegment(sketch, "E204.MirrorCS", {"start": v(1879.6, 464.31) * mm, "end": v(1955.8, 464.31) * mm});
            skLineSegment(sketch, "E205.MirrorCS", {"start": v(1879.6, 500.89) * mm, "end": v(1955.8, 500.89) * mm});
            skLineSegment(sketch, "E206.MirrorCS", {"start": v(1879.6, 464.31) * mm, "end": v(1879.6, 500.89) * mm});
            skLineSegment(sketch, "E207.MirrorCS", {"start": v(1955.8, 464.31) * mm, "end": v(1955.8, 500.89) * mm});
            skLineSegment(sketch, "E208.MirrorCS", {"start": v(1215.83, 500.89) * mm, "end": v(1292.03, 500.89) * mm});
            skLineSegment(sketch, "E209.MirrorCS", {"start": v(1215.83, 464.31) * mm, "end": v(1292.03, 464.31) * mm});
            skLineSegment(sketch, "E210.MirrorCS", {"start": v(1215.83, 464.31) * mm, "end": v(1215.83, 500.89) * mm});
            skLineSegment(sketch, "E211.MirrorCS", {"start": v(1292.03, 464.31) * mm, "end": v(1292.03, 500.89) * mm});
            skLineSegment(sketch, "E212.bottom", {"start": v(-50.8, 2359.6) * mm, "end": v(-69.09, 2359.6) * mm});
            skLineSegment(sketch, "E212.top", {"start": v(-50.8, 2181.8) * mm, "end": v(-69.09, 2181.8) * mm});
            skLineSegment(sketch, "E212.left", {"start": v(-50.8, 2359.6) * mm, "end": v(-50.8, 2181.8) * mm});
            skLineSegment(sketch, "E212.right", {"start": v(-69.09, 2359.6) * mm, "end": v(-69.09, 2181.8) * mm});
            skPoint(sketch, "E212.middle", {"position": v(-59.94, 2270.7) * mm});
            skLineSegment(sketch, "E213.MirrorCS", {"start": v(-838.2, 2181.8) * mm, "end": v(-819.91, 2181.8) * mm});
            skLineSegment(sketch, "E214.MirrorCS", {"start": v(-838.2, 2359.6) * mm, "end": v(-819.91, 2359.6) * mm});
            skLineSegment(sketch, "E215.MirrorCS", {"start": v(-819.91, 2359.6) * mm, "end": v(-819.91, 2181.8) * mm});
            skLineSegment(sketch, "E216.MirrorCS", {"start": v(-838.2, 2359.6) * mm, "end": v(-838.2, 2181.8) * mm});
            skPoint(sketch, "E217.MirrorP", {"position": v(-829.06, 2270.7) * mm});
            skLineSegment(sketch, "E218.MirrorCS", {"start": v(-50.8, 790) * mm, "end": v(-69.09, 790) * mm});
            skLineSegment(sketch, "E219.MirrorCS", {"start": v(-838.2, 967.8) * mm, "end": v(-819.91, 967.8) * mm});
            skLineSegment(sketch, "E220.MirrorCS", {"start": v(-838.2, 790) * mm, "end": v(-819.91, 790) * mm});
            skLineSegment(sketch, "E221.MirrorCS", {"start": v(-50.8, 967.8) * mm, "end": v(-69.09, 967.8) * mm});
            skLineSegment(sketch, "E222.MirrorCS", {"start": v(-50.8, 790) * mm, "end": v(-50.8, 967.8) * mm});
            skLineSegment(sketch, "E223.MirrorCS", {"start": v(-69.09, 790) * mm, "end": v(-69.09, 967.8) * mm});
            skLineSegment(sketch, "E224.MirrorCS", {"start": v(-819.91, 790) * mm, "end": v(-819.91, 967.8) * mm});
            skLineSegment(sketch, "E225.MirrorCS", {"start": v(-838.2, 790) * mm, "end": v(-838.2, 967.8) * mm});
            skPoint(sketch, "E226.MirrorP", {"position": v(-59.94, 878.9) * mm});
            skPoint(sketch, "E227.MirrorP", {"position": v(-829.06, 878.9) * mm});
            skLineSegment(sketch, "E228.MirrorCS", {"start": v(-838.2, 1473.2) * mm, "end": v(-819.91, 1473.2) * mm});
            skLineSegment(sketch, "E229.MirrorCS", {"start": v(-838.2, 1676.4) * mm, "end": v(-819.91, 1676.4) * mm});
            skPoint(sketch, "E230.MirrorP", {"position": v(-829.06, 1574.8) * mm});
            skLineSegment(sketch, "E231.MirrorCS", {"start": v(-819.91, 1676.4) * mm, "end": v(-819.91, 1473.2) * mm});
            skLineSegment(sketch, "E232.MirrorCS", {"start": v(-838.2, 1676.4) * mm, "end": v(-838.2, 1473.2) * mm});
            skPoint(sketch, "E233", {"position": v(2797.37, 482.6) * mm});
            skPoint(sketch, "E234", {"position": v(2797.37, 321.5) * mm});
            skLineSegment(sketch, "E235", {"start": v(1117.6, -145.29) * mm, "end": v(1117.6, -464.31) * mm});
            skLineSegment(sketch, "E236", {"start": v(1117.6, -464.31) * mm, "end": v(2895.6, -464.31) * mm});
            skLineSegment(sketch, "E237", {"start": v(2895.6, -464.31) * mm, "end": v(2895.6, -145.29) * mm});
            skLineSegment(sketch, "E238.bottom", {"start": v(1549.4, -369.89) * mm, "end": v(2463.8, -369.89) * mm});
            skLineSegment(sketch, "E238.top", {"start": v(1549.4, -208.79) * mm, "end": v(2463.8, -208.79) * mm});
            skLineSegment(sketch, "E238.left", {"start": v(1549.4, -369.89) * mm, "end": v(1549.4, -208.79) * mm});
            skLineSegment(sketch, "E238.right", {"start": v(2463.8, -369.89) * mm, "end": v(2463.8, -208.79) * mm});
            skLineSegment(sketch, "E239.0", {"start": v(2882.5, 378.48) * mm, "end": v(1114.88, -25.55) * mm, "construction": true});
            skLineSegment(sketch, "E240", {"start": v(1215.83, -163.58) * mm, "end": v(1215.83, -2.48) * mm, "construction": true});
            skLineSegment(sketch, "E241", {"start": v(1215.83, -83.03) * mm, "end": v(1117.6, -83.03) * mm, "construction": true});
            skLineSegment(sketch, "E242", {"start": v(1206.69, 91.95) * mm, "end": v(1206.69, -83.03) * mm, "construction": true});
            skLineSegment(sketch, "E243", {"start": v(716.79, 1199.39) * mm, "end": v(716.79, 1574.8) * mm, "construction": true});
            skLineSegment(sketch, "E244", {"start": v(-444.5, 1574.8) * mm, "end": v(-69.09, 1574.8) * mm, "construction": true});
            skLineSegment(sketch, "E245", {"start": v(2006.6, -417.1) * mm, "end": v(2382.01, -417.1) * mm, "construction": true});
            skLineSegment(sketch, "E246", {"start": v(2006.6, -369.89) * mm, "end": v(2006.6, -464.31) * mm, "construction": true});
            skLineSegment(sketch, "E247.bottom", {"start": v(2382.01, -464.31) * mm, "end": v(2400.3, -464.31) * mm});
            skLineSegment(sketch, "E247.top", {"start": v(2382.01, -438.91) * mm, "end": v(2400.3, -438.91) * mm});
            skLineSegment(sketch, "E247.left", {"start": v(2382.01, -464.31) * mm, "end": v(2382.01, -438.91) * mm});
            skLineSegment(sketch, "E247.right", {"start": v(2400.3, -464.31) * mm, "end": v(2400.3, -438.91) * mm});
            skPoint(sketch, "E248.endSnap0", {"position": v(2463.8, -289.34) * mm});
            skLineSegment(sketch, "E249", {"start": v(2391.16, -464.31) * mm, "end": v(2391.16, -289.34) * mm, "construction": true});
            skLineSegment(sketch, "E250.MirrorCS", {"start": v(1612.9, -464.31) * mm, "end": v(1612.9, -438.91) * mm});
            skLineSegment(sketch, "E251.MirrorCS", {"start": v(1631.19, -464.31) * mm, "end": v(1631.19, -438.91) * mm});
            skLineSegment(sketch, "E252.MirrorCS", {"start": v(1631.19, -464.31) * mm, "end": v(1612.9, -464.31) * mm});
            skLineSegment(sketch, "E253.MirrorCS", {"start": v(1631.19, -438.91) * mm, "end": v(1612.9, -438.91) * mm});
            skLineSegment(sketch, "E254.bottom", {"start": v(1117.6, -464.31) * mm, "end": v(1099.31, -464.31) * mm});
            skLineSegment(sketch, "E254.top", {"start": v(1117.6, -413.51) * mm, "end": v(1099.31, -413.51) * mm});
            skLineSegment(sketch, "E254.left", {"start": v(1117.6, -464.31) * mm, "end": v(1117.6, -413.51) * mm});
            skLineSegment(sketch, "E254.right", {"start": v(1099.31, -464.31) * mm, "end": v(1099.31, -413.51) * mm});
            skLineSegment(sketch, "E255.bottom", {"start": v(1117.6, -145.29) * mm, "end": v(1099.31, -145.29) * mm});
            skLineSegment(sketch, "E255.top", {"start": v(1117.6, -196.09) * mm, "end": v(1099.31, -196.09) * mm});
            skLineSegment(sketch, "E255.left", {"start": v(1117.6, -145.29) * mm, "end": v(1117.6, -196.09) * mm});
            skLineSegment(sketch, "E255.right", {"start": v(1099.31, -145.29) * mm, "end": v(1099.31, -196.09) * mm});
            skLineSegment(sketch, "E256.MirrorCS", {"start": v(2895.6, -464.31) * mm, "end": v(2913.89, -464.31) * mm});
            skLineSegment(sketch, "E257.MirrorCS", {"start": v(2895.6, -413.51) * mm, "end": v(2913.89, -413.51) * mm});
            skLineSegment(sketch, "E258.MirrorCS", {"start": v(2895.6, -464.31) * mm, "end": v(2895.6, -413.51) * mm});
            skLineSegment(sketch, "E259.MirrorCS", {"start": v(2913.89, -464.31) * mm, "end": v(2913.89, -413.51) * mm});
            skLineSegment(sketch, "E260.MirrorCS", {"start": v(2913.89, -145.29) * mm, "end": v(2913.89, -196.09) * mm});
            skLineSegment(sketch, "E261.MirrorCS", {"start": v(2895.6, -196.09) * mm, "end": v(2913.89, -196.09) * mm});
            skLineSegment(sketch, "E262.bottom", {"start": v(870.71, -464.31) * mm, "end": v(889, -464.31) * mm});
            skLineSegment(sketch, "E262.top", {"start": v(870.71, -413.51) * mm, "end": v(889, -413.51) * mm});
            skLineSegment(sketch, "E262.left", {"start": v(870.71, -464.31) * mm, "end": v(870.71, -413.51) * mm});
            skLineSegment(sketch, "E262.right", {"start": v(889, -464.31) * mm, "end": v(889, -413.51) * mm});
            skLineSegment(sketch, "E263.bottom", {"start": v(870.71, -145.29) * mm, "end": v(889, -145.29) * mm});
            skLineSegment(sketch, "E263.top", {"start": v(870.71, -196.09) * mm, "end": v(889, -196.09) * mm});
            skLineSegment(sketch, "E263.left", {"start": v(870.71, -145.29) * mm, "end": v(870.71, -196.09) * mm});
            skLineSegment(sketch, "E263.right", {"start": v(889, -145.29) * mm, "end": v(889, -196.09) * mm});
            skLineSegment(sketch, "E264.MirrorCS", {"start": v(-889, -145.29) * mm, "end": v(-889, -196.09) * mm});
            skLineSegment(sketch, "E265.MirrorCS", {"start": v(-870.71, -145.29) * mm, "end": v(-870.71, -196.09) * mm});
            skLineSegment(sketch, "E266.MirrorCS", {"start": v(-870.71, -196.09) * mm, "end": v(-889, -196.09) * mm});
            skLineSegment(sketch, "E267.MirrorCS", {"start": v(-870.71, -464.31) * mm, "end": v(-889, -464.31) * mm});
            skLineSegment(sketch, "E268.MirrorCS", {"start": v(-889, -464.31) * mm, "end": v(-889, -413.51) * mm});
            skLineSegment(sketch, "E269.MirrorCS", {"start": v(-870.71, -464.31) * mm, "end": v(-870.71, -413.51) * mm});
            skLineSegment(sketch, "E270.MirrorCS", {"start": v(-870.71, -413.51) * mm, "end": v(-889, -413.51) * mm});
            skLineSegment(sketch, "E271.bottom", {"start": v(-889, 879.28) * mm, "end": v(-870.71, 879.28) * mm});
            skLineSegment(sketch, "E271.top", {"start": v(-889, 764.98) * mm, "end": v(-870.71, 764.98) * mm});
            skLineSegment(sketch, "E271.left", {"start": v(-889, 879.28) * mm, "end": v(-889, 764.98) * mm});
            skLineSegment(sketch, "E271.right", {"start": v(-870.71, 879.28) * mm, "end": v(-870.71, 764.98) * mm});
            skPoint(sketch, "E271.middle", {"position": v(-879.86, 822.13) * mm});
            skLineSegment(sketch, "E272.bottom", {"start": v(-889, 1428.75) * mm, "end": v(-870.71, 1428.75) * mm});
            skLineSegment(sketch, "E272.top", {"start": v(-889, 1543.05) * mm, "end": v(-870.71, 1543.05) * mm});
            skLineSegment(sketch, "E272.left", {"start": v(-889, 1428.75) * mm, "end": v(-889, 1543.05) * mm});
            skLineSegment(sketch, "E272.right", {"start": v(-870.71, 1428.75) * mm, "end": v(-870.71, 1543.05) * mm});
            skPoint(sketch, "E272.middle", {"position": v(-879.86, 1485.9) * mm});
            skLineSegment(sketch, "E273", {"start": v(-879.86, 822.13) * mm, "end": v(-879.86, 685.8) * mm, "construction": true});
            skLineSegment(sketch, "E274", {"start": v(-879.86, 1485.9) * mm, "end": v(-879.86, 685.8) * mm, "construction": true});
            skLineSegment(sketch, "E275", {"start": v(1117.6, 500.89) * mm, "end": v(1253.93, 500.89) * mm, "construction": true});
            skLineSegment(sketch, "E276", {"start": v(1117.6, 500.89) * mm, "end": v(1917.7, 500.89) * mm, "construction": true});
            skLineSegment(sketch, "E277.MirrorCS", {"start": v(0, 879.28) * mm, "end": v(-18.29, 879.28) * mm});
            skLineSegment(sketch, "E278.MirrorCS", {"start": v(0, 879.28) * mm, "end": v(0, 764.98) * mm});
            skLineSegment(sketch, "E279.MirrorCS", {"start": v(-18.29, 1428.75) * mm, "end": v(-18.29, 1543.05) * mm});
            skPoint(sketch, "E280.MirrorP", {"position": v(-9.14, 1485.9) * mm});
            skLineSegment(sketch, "E281.MirrorCS", {"start": v(0, 1428.75) * mm, "end": v(0, 1543.05) * mm});
            skPoint(sketch, "E282.MirrorP", {"position": v(-9.14, 822.13) * mm});
            skLineSegment(sketch, "E283.MirrorCS", {"start": v(0, 1543.05) * mm, "end": v(-18.29, 1543.05) * mm});
            skLineSegment(sketch, "E284.MirrorCS", {"start": v(0, 764.98) * mm, "end": v(-18.29, 764.98) * mm});
            skLineSegment(sketch, "E285.MirrorCS", {"start": v(0, 1428.75) * mm, "end": v(-18.29, 1428.75) * mm});
            skLineSegment(sketch, "E286.MirrorCS", {"start": v(-18.29, 879.28) * mm, "end": v(-18.29, 764.98) * mm});
            skLineSegment(sketch, "E287.MirrorCS", {"start": v(-889, 2270.32) * mm, "end": v(-870.71, 2270.32) * mm});
            skLineSegment(sketch, "E288.MirrorCS", {"start": v(-889, 2384.62) * mm, "end": v(-870.71, 2384.62) * mm});
            skLineSegment(sketch, "E289.MirrorCS", {"start": v(-889, 2270.32) * mm, "end": v(-889, 2384.62) * mm});
            skLineSegment(sketch, "E290.MirrorCS", {"start": v(-870.71, 2270.32) * mm, "end": v(-870.71, 2384.62) * mm});
            skLineSegment(sketch, "E291.MirrorCS", {"start": v(-889, 1720.85) * mm, "end": v(-870.71, 1720.85) * mm});
            skLineSegment(sketch, "E292.MirrorCS", {"start": v(-889, 1606.55) * mm, "end": v(-870.71, 1606.55) * mm});
            skPoint(sketch, "E293.MirrorP", {"position": v(-879.86, 2327.47) * mm});
            skLineSegment(sketch, "E294.MirrorCS", {"start": v(-889, 1720.85) * mm, "end": v(-889, 1606.55) * mm});
            skPoint(sketch, "E295.MirrorP", {"position": v(-879.86, 1663.7) * mm});
            skLineSegment(sketch, "E296.MirrorCS", {"start": v(-870.71, 1720.85) * mm, "end": v(-870.71, 1606.55) * mm});
            skLineSegment(sketch, "E297.MirrorCS", {"start": v(0, 1720.85) * mm, "end": v(-18.29, 1720.85) * mm});
            skLineSegment(sketch, "E298.MirrorCS", {"start": v(0, 2384.62) * mm, "end": v(-18.29, 2384.62) * mm});
            skLineSegment(sketch, "E299.MirrorCS", {"start": v(0, 2270.32) * mm, "end": v(-18.29, 2270.32) * mm});
            skLineSegment(sketch, "E300.MirrorCS", {"start": v(0, 1606.55) * mm, "end": v(-18.29, 1606.55) * mm});
            skLineSegment(sketch, "E301.MirrorCS", {"start": v(0, 1720.85) * mm, "end": v(0, 1606.55) * mm});
            skLineSegment(sketch, "E302.MirrorCS", {"start": v(-18.29, 1720.85) * mm, "end": v(-18.29, 1606.55) * mm});
            skLineSegment(sketch, "E303.MirrorCS", {"start": v(-18.29, 2270.32) * mm, "end": v(-18.29, 2384.62) * mm});
            skLineSegment(sketch, "E304.MirrorCS", {"start": v(0, 2270.32) * mm, "end": v(0, 2384.62) * mm});
            skPoint(sketch, "E305.MirrorP", {"position": v(-9.14, 2327.47) * mm});
            skPoint(sketch, "E306.MirrorP", {"position": v(-9.14, 1663.7) * mm});
            skLineSegment(sketch, "E307.0", {"start": v(-889, 692.15) * mm, "end": v(0, 692.15) * mm, "construction": true});
            skLineSegment(sketch, "E308.bottom", {"start": v(228.6, 1117.6) * mm, "end": v(210.31, 1117.6) * mm});
            skLineSegment(sketch, "E308.top", {"start": v(228.6, 1193.8) * mm, "end": v(210.31, 1193.8) * mm});
            skLineSegment(sketch, "E308.left", {"start": v(228.6, 1117.6) * mm, "end": v(228.6, 1193.8) * mm});
            skLineSegment(sketch, "E308.right", {"start": v(210.31, 1117.6) * mm, "end": v(210.31, 1193.8) * mm});
            skPoint(sketch, "E308.middle", {"position": v(219.46, 1155.7) * mm});
            skLineSegment(sketch, "E309.MirrorCS", {"start": v(228.6, 1955.8) * mm, "end": v(210.31, 1955.8) * mm});
            skLineSegment(sketch, "E310.MirrorCS", {"start": v(228.6, 2032) * mm, "end": v(210.31, 2032) * mm});
            skLineSegment(sketch, "E311.MirrorCS", {"start": v(210.31, 2032) * mm, "end": v(210.31, 1955.8) * mm});
            skPoint(sketch, "E312.MirrorP", {"position": v(219.46, 1993.9) * mm});
            skLineSegment(sketch, "E313.MirrorCS", {"start": v(228.6, 2032) * mm, "end": v(228.6, 1955.8) * mm});
            skLineSegment(sketch, "E314.bottom", {"start": v(-292.1, 1098.55) * mm, "end": v(-310.39, 1098.55) * mm});
            skLineSegment(sketch, "E314.top", {"start": v(-292.1, 1212.85) * mm, "end": v(-310.39, 1212.85) * mm});
            skLineSegment(sketch, "E314.left", {"start": v(-292.1, 1098.55) * mm, "end": v(-292.1, 1212.85) * mm});
            skLineSegment(sketch, "E314.right", {"start": v(-310.39, 1098.55) * mm, "end": v(-310.39, 1212.85) * mm});
            skPoint(sketch, "E314.middle", {"position": v(-301.24, 1155.7) * mm});
            skPoint(sketch, "E314.middle.positionSnap0", {"position": v(-301.24, 464.31) * mm});
            skPoint(sketch, "E314.middle.positionSnap1", {"position": v(210.31, 1155.7) * mm});
            skPoint(sketch, "E314.centerSnap0", {"position": v(-301.24, 464.31) * mm});
            skPoint(sketch, "E314.centerSnap1", {"position": v(210.31, 1155.7) * mm});
            skLineSegment(sketch, "E315.MirrorCS", {"start": v(-596.9, 1212.85) * mm, "end": v(-578.61, 1212.85) * mm});
            skLineSegment(sketch, "E316.MirrorCS", {"start": v(-596.9, 1098.55) * mm, "end": v(-578.61, 1098.55) * mm});
            skLineSegment(sketch, "E317.MirrorCS", {"start": v(-596.9, 1098.55) * mm, "end": v(-596.9, 1212.85) * mm});
            skLineSegment(sketch, "E318.MirrorCS", {"start": v(-578.61, 1098.55) * mm, "end": v(-578.61, 1212.85) * mm});
            skPoint(sketch, "E319.MirrorP", {"position": v(-587.76, 1155.7) * mm});
            skLineSegment(sketch, "E320.MirrorCS", {"start": v(-292.1, 2051.05) * mm, "end": v(-310.39, 2051.05) * mm});
            skLineSegment(sketch, "E321.MirrorCS", {"start": v(-292.1, 1936.75) * mm, "end": v(-310.39, 1936.75) * mm});
            skLineSegment(sketch, "E322.MirrorCS", {"start": v(-596.9, 2051.05) * mm, "end": v(-578.61, 2051.05) * mm});
            skLineSegment(sketch, "E323.MirrorCS", {"start": v(-596.9, 1936.75) * mm, "end": v(-578.61, 1936.75) * mm});
            skLineSegment(sketch, "E324.MirrorCS", {"start": v(-292.1, 2051.05) * mm, "end": v(-292.1, 1936.75) * mm});
            skLineSegment(sketch, "E325.MirrorCS", {"start": v(-596.9, 2051.05) * mm, "end": v(-596.9, 1936.75) * mm});
            skLineSegment(sketch, "E326.MirrorCS", {"start": v(-578.61, 2051.05) * mm, "end": v(-578.61, 1936.75) * mm});
            skLineSegment(sketch, "E327.MirrorCS", {"start": v(-310.39, 2051.05) * mm, "end": v(-310.39, 1936.75) * mm});
            skPoint(sketch, "E328.MirrorP", {"position": v(-301.24, 1993.9) * mm});
            skPoint(sketch, "E329.MirrorP", {"position": v(-587.76, 1993.9) * mm});
            skLineSegment(sketch, "E330", {"start": v(2133.6, 169.78) * mm, "end": v(2133.6, 482.6) * mm, "construction": true});
            skLineSegment(sketch, "E331", {"start": v(1727.2, -464.31) * mm, "end": v(1727.2, 464.31) * mm, "construction": true});
            skCircle(sketch, "E332", {"center": v(1727.2, 362.71) * mm, "radius": 3.5 * mm});
            skCircle(sketch, "E333", {"center": v(1727.2, -43.69) * mm, "radius": 3.5 * mm});
            skLineSegment(sketch, "E334", {"start": v(1727.2, -145.29) * mm, "end": v(1727.2, -208.79) * mm, "construction": true});
            skCircle(sketch, "E335", {"center": v(1727.2, -177.04) * mm, "radius": 3.5 * mm});
            skLineSegment(sketch, "E336", {"start": v(1727.2, -464.31) * mm, "end": v(1727.2, -369.89) * mm, "construction": true});
            skCircle(sketch, "E337", {"center": v(1727.2, -417.1) * mm, "radius": 3.5 * mm});
            skCircle(sketch, "E338.MirrorC", {"center": v(2286, 362.71) * mm, "radius": 3.5 * mm});
            skCircle(sketch, "E339.MirrorC", {"center": v(2286, -43.69) * mm, "radius": 3.5 * mm});
            skCircle(sketch, "E340.MirrorC", {"center": v(2286, -177.04) * mm, "radius": 3.5 * mm});
            skCircle(sketch, "E341.MirrorC", {"center": v(2286, -417.1) * mm, "radius": 3.5 * mm});
            skLineSegment(sketch, "E342.bottom", {"start": v(2939.29, -196.09) * mm, "end": v(2957.58, -196.09) * mm});
            skLineSegment(sketch, "E342.top", {"start": v(2939.29, -413.51) * mm, "end": v(2957.58, -413.51) * mm});
            skLineSegment(sketch, "E342.left", {"start": v(2939.29, -196.09) * mm, "end": v(2939.29, -413.51) * mm});
            skLineSegment(sketch, "E342.right", {"start": v(2957.58, -196.09) * mm, "end": v(2957.58, -413.51) * mm});
            skLineSegment(sketch, "E343.bottom", {"start": v(2957.58, -464.31) * mm, "end": v(2975.86, -464.31) * mm});
            skLineSegment(sketch, "E343.top", {"start": v(2957.58, -145.29) * mm, "end": v(2975.86, -145.29) * mm});
            skLineSegment(sketch, "E343.left", {"start": v(2957.58, -464.31) * mm, "end": v(2957.58, -145.29) * mm});
            skLineSegment(sketch, "E343.right", {"start": v(2975.86, -464.31) * mm, "end": v(2975.86, -145.29) * mm});
            skLineSegment(sketch, "E344.bottom", {"start": v(279.4, 2507.49) * mm, "end": v(838.2, 2507.49) * mm});
            skLineSegment(sketch, "E344.top", {"start": v(279.4, 2525.78) * mm, "end": v(838.2, 2525.78) * mm});
            skLineSegment(sketch, "E344.left", {"start": v(279.4, 2507.49) * mm, "end": v(279.4, 2525.78) * mm});
            skLineSegment(sketch, "E344.right", {"start": v(838.2, 2507.49) * mm, "end": v(838.2, 2525.78) * mm});
            skLineSegment(sketch, "E345.bottom", {"start": v(889, 2525.78) * mm, "end": v(228.6, 2525.78) * mm});
            skLineSegment(sketch, "E345.top", {"start": v(889, 2544.06) * mm, "end": v(228.6, 2544.06) * mm});
            skLineSegment(sketch, "E345.left", {"start": v(889, 2525.78) * mm, "end": v(889, 2544.06) * mm});
            skLineSegment(sketch, "E345.right", {"start": v(228.6, 2525.78) * mm, "end": v(228.6, 2544.06) * mm});
            skLineSegment(sketch, "E346", {"start": v(-310.39, 134.11) * mm, "end": v(-870.71, 134.11) * mm, "construction": true});
            skLineSegment(sketch, "E347", {"start": v(-292.1, 134.11) * mm, "end": v(292.1, 134.11) * mm, "construction": true});
            skLineSegment(sketch, "E348.bottom", {"start": v(-615.95, 508) * mm, "end": v(-565.15, 508) * mm});
            skLineSegment(sketch, "E348.top", {"start": v(-615.95, 482.6) * mm, "end": v(-565.15, 482.6) * mm});
            skLineSegment(sketch, "E348.left", {"start": v(-615.95, 508) * mm, "end": v(-615.95, 482.6) * mm});
            skLineSegment(sketch, "E348.right", {"start": v(-565.15, 508) * mm, "end": v(-565.15, 482.6) * mm});
            skPoint(sketch, "E348.middle", {"position": v(-590.55, 495.3) * mm});
            skPoint(sketch, "E348.middle.positionSnap0", {"position": v(-590.55, 134.11) * mm});
            skPoint(sketch, "E348.centerSnap0", {"position": v(-590.55, 134.11) * mm});
            skLineSegment(sketch, "E349.bottom", {"start": v(-25.4, 508) * mm, "end": v(25.4, 508) * mm});
            skLineSegment(sketch, "E349.top", {"start": v(-25.4, 482.6) * mm, "end": v(25.4, 482.6) * mm});
            skLineSegment(sketch, "E349.left", {"start": v(-25.4, 508) * mm, "end": v(-25.4, 482.6) * mm});
            skLineSegment(sketch, "E349.right", {"start": v(25.4, 508) * mm, "end": v(25.4, 482.6) * mm});
            skPoint(sketch, "E349.middle", {"position": v(0, 495.3) * mm});
            skLineSegment(sketch, "E350.MirrorCS", {"start": v(565.15, 508) * mm, "end": v(565.15, 482.6) * mm});
            skLineSegment(sketch, "E351.MirrorCS", {"start": v(615.95, 508) * mm, "end": v(615.95, 482.6) * mm});
            skLineSegment(sketch, "E352.MirrorCS", {"start": v(615.95, 482.6) * mm, "end": v(565.15, 482.6) * mm});
            skLineSegment(sketch, "E353.MirrorCS", {"start": v(615.95, 508) * mm, "end": v(565.15, 508) * mm});
            skPoint(sketch, "E354.MirrorP", {"position": v(590.55, 495.3) * mm});
            skLineSegment(sketch, "E355.MirrorCS", {"start": v(-615.95, -508) * mm, "end": v(-565.15, -508) * mm});
            skLineSegment(sketch, "E356.MirrorCS", {"start": v(-615.95, -482.6) * mm, "end": v(-565.15, -482.6) * mm});
            skLineSegment(sketch, "E357.MirrorCS", {"start": v(-615.95, -508) * mm, "end": v(-615.95, -482.6) * mm});
            skLineSegment(sketch, "E358.MirrorCS", {"start": v(-565.15, -508) * mm, "end": v(-565.15, -482.6) * mm});
            skPoint(sketch, "E359.MirrorP", {"position": v(-590.55, -495.3) * mm});
            skLineSegment(sketch, "E360.MirrorCS", {"start": v(-25.4, -508) * mm, "end": v(25.4, -508) * mm});
            skLineSegment(sketch, "E361.MirrorCS", {"start": v(-25.4, -482.6) * mm, "end": v(25.4, -482.6) * mm});
            skLineSegment(sketch, "E362.MirrorCS", {"start": v(-25.4, -508) * mm, "end": v(-25.4, -482.6) * mm});
            skPoint(sketch, "E363.MirrorP", {"position": v(0, -495.3) * mm});
            skLineSegment(sketch, "E364.MirrorCS", {"start": v(25.4, -508) * mm, "end": v(25.4, -482.6) * mm});
            skLineSegment(sketch, "E365.MirrorCS", {"start": v(615.95, -508) * mm, "end": v(565.15, -508) * mm});
            skLineSegment(sketch, "E366.MirrorCS", {"start": v(615.95, -482.6) * mm, "end": v(565.15, -482.6) * mm});
            skPoint(sketch, "E367.MirrorP", {"position": v(590.55, -495.3) * mm});
            skLineSegment(sketch, "E368.MirrorCS", {"start": v(615.95, -508) * mm, "end": v(615.95, -482.6) * mm});
            skLineSegment(sketch, "E369.MirrorCS", {"start": v(565.15, -508) * mm, "end": v(565.15, -482.6) * mm});
            skLineSegment(sketch, "E370.bottom", {"start": v(889, 362.71) * mm, "end": v(870.71, 362.71) * mm});
            skLineSegment(sketch, "E370.top", {"start": v(889, 311.91) * mm, "end": v(870.71, 311.91) * mm});
            skLineSegment(sketch, "E370.left", {"start": v(889, 362.71) * mm, "end": v(889, 311.91) * mm});
            skLineSegment(sketch, "E370.right", {"start": v(870.71, 362.71) * mm, "end": v(870.71, 311.91) * mm});
            skLineSegment(sketch, "E371.MirrorCS", {"start": v(-870.71, 362.71) * mm, "end": v(-870.71, 311.91) * mm});
            skLineSegment(sketch, "E372.MirrorCS", {"start": v(-889, 362.71) * mm, "end": v(-889, 311.91) * mm});
            skLineSegment(sketch, "E373.MirrorCS", {"start": v(-889, 311.91) * mm, "end": v(-870.71, 311.91) * mm});
            skLineSegment(sketch, "E374.MirrorCS", {"start": v(-889, 362.71) * mm, "end": v(-870.71, 362.71) * mm});
            skSolve(sketch);
        }
        {
            var Q0;
            {var subQ25=sQuery(id+"F1.wireOp",EDGE,"E45.bottom");Q0=makeQuery(id+"F1.imprint","IMPRINT",FACE,{"disambiguationData":[TD([[makeQuery(id+"F1.imprint","IMPRINT",EDGE,{"derivedFrom":subQ25}),1.0]])]});}
            var Q1;
            Q1=makeQuery(id+"F1.imprint","IMPRINT",FACE,{"disambiguationData":[TD([[makeQuery(id+"F1.imprint","IMPRINT",EDGE,{"derivedFrom":sQuery(id+"F1.wireOp",EDGE,"E52.MirrorCS")}),-1.0]])]});
            var Q2;
            Q2=makeQuery(id+"F1.imprint","IMPRINT",FACE,{"disambiguationData":[TD([[makeQuery(id+"F1.imprint","IMPRINT",EDGE,{"derivedFrom":sQuery(id+"F1.wireOp",EDGE,"E56.MirrorCS")}),-1.0]])]});
            var Q3;
            Q3=makeQuery(id+"F1.imprint","IMPRINT",FACE,{"disambiguationData":[TD([[makeQuery(id+"F1.imprint","IMPRINT",EDGE,{"derivedFrom":sQuery(id+"F1.wireOp",EDGE,"E48.MirrorCS")}),-1.0]])]});
            var Q4;
            Q4=makeQuery(id+"F1.imprint","IMPRINT",FACE,{"disambiguationData":[TD([[makeQuery(id+"F1.imprint","IMPRINT",EDGE,{"derivedFrom":sQuery(id+"F1.wireOp",EDGE,"E45.bottom")}),-1.0]])]});
            var Q5;
            Q5=makeQuery(id+"F1.imprint","IMPRINT",FACE,{"disambiguationData":[TD([[makeQuery(id+"F1.imprint","IMPRINT",EDGE,{"derivedFrom":sQuery(id+"F1.wireOp",EDGE,"E63.bottom")}),1.0]])]});
            var Q6;
            Q6=makeQuery(id+"F1.imprint","IMPRINT",FACE,{"disambiguationData":[TD([[makeQuery(id+"F1.imprint","IMPRINT",EDGE,{"derivedFrom":sQuery(id+"F1.wireOp",EDGE,"E64.bottom")}),-1.0]])]});
            var Q7;
            Q7=makeQuery(id+"F1.imprint","IMPRINT",FACE,{"disambiguationData":[TD([[makeQuery(id+"F1.imprint","IMPRINT",EDGE,{"derivedFrom":sQuery(id+"F1.wireOp",EDGE,"E67.MirrorCS")}),1.0]])]});
            var Q8;
            Q8=makeQuery(id+"F1.imprint","IMPRINT",FACE,{"disambiguationData":[TD([[makeQuery(id+"F1.imprint","IMPRINT",EDGE,{"derivedFrom":sQuery(id+"F1.wireOp",EDGE,"E308.bottom")}),-1.0]])]});
            var Q9;
            Q9=makeQuery(id+"F1.imprint","IMPRINT",FACE,{"disambiguationData":[TD([[makeQuery(id+"F1.imprint","IMPRINT",EDGE,{"derivedFrom":sQuery(id+"F1.wireOp",EDGE,"E309.MirrorCS")}),-1.0]])]});
            var Q10;
            Q10=makeQuery(id+"F1.imprint","IMPRINT",FACE,{"disambiguationData":[TD([[makeQuery(id+"F1.imprint","IMPRINT",EDGE,{"derivedFrom":sQuery(id+"F1.wireOp",EDGE,"E345.top")}),1.0]])]});
            var Q11;
            Q11=makeQuery(id+"F1.imprint","IMPRINT",FACE,{"disambiguationData":[TD([[makeQuery(id+"F1.imprint","IMPRINT",EDGE,{"derivedFrom":sQuery(id+"F1.wireOp",EDGE,"E344.bottom")}),1.0]])]});
            var Q12;
            Q12=makeQuery(id+"F1.imprint","IMPRINT",FACE,{"disambiguationData":[TD([[makeQuery(id+"F1.imprint","IMPRINT",EDGE,{"derivedFrom":sQuery(id+"F1.wireOp",EDGE,"E75.MirrorCS")}),-1.0]])]});
            var Q13;
            Q13=makeQuery(id+"F1.imprint","IMPRINT",FACE,{"disambiguationData":[TD([[makeQuery(id+"F1.imprint","IMPRINT",EDGE,{"derivedFrom":sQuery(id+"F1.wireOp",EDGE,"E71.MirrorCS")}),1.0]])]});
            var Q14;
            {var subQ14=sQuery(id+"F1.wireOp",EDGE,"E0.left");Q14=makeQuery(id+"F1.imprint","IMPRINT",FACE,{"disambiguationData":[TD([[makeQuery(id+"F1.imprint","IMPRINT",EDGE,{"derivedFrom":subQ14}),-1.0]])]});}
            var Q15;
            {var subQ8=sQuery(id+"F1.wireOp",EDGE,"E87");Q15=makeQuery(id+"F1.imprint","IMPRINT",FACE,{"disambiguationData":[TD([[makeQuery(id+"F1.imprint","IMPRINT",EDGE,{"derivedFrom":subQ8}),-1.0]])]});}
            var Q16;
            Q16=makeQuery(id+"F1.imprint","IMPRINT",FACE,{"disambiguationData":[TD([[makeQuery(id+"F1.imprint","IMPRINT",EDGE,{"derivedFrom":sQuery(id+"F1.wireOp",EDGE,"E208.MirrorCS")}),-1.0]])]});
            var Q17;
            Q17=makeQuery(id+"F1.imprint","IMPRINT",FACE,{"disambiguationData":[TD([[makeQuery(id+"F1.imprint","IMPRINT",EDGE,{"derivedFrom":sQuery(id+"F1.wireOp",EDGE,"E110.bottom")}),1.0]])]});
            var Q18;
            Q18=makeQuery(id+"F1.imprint","IMPRINT",FACE,{"disambiguationData":[TD([[makeQuery(id+"F1.imprint","IMPRINT",EDGE,{"derivedFrom":sQuery(id+"F1.wireOp",EDGE,"E111.bottom")}),-1.0]])]});
            var Q19;
            Q19=makeQuery(id+"F1.imprint","IMPRINT",FACE,{"disambiguationData":[TD([[makeQuery(id+"F1.imprint","IMPRINT",EDGE,{"derivedFrom":sQuery(id+"F1.wireOp",EDGE,"E255.bottom")}),1.0]])]});
            var Q20;
            Q20=makeQuery(id+"F1.imprint","IMPRINT",FACE,{"disambiguationData":[TD([[makeQuery(id+"F1.imprint","IMPRINT",EDGE,{"derivedFrom":sQuery(id+"F1.wireOp",EDGE,"E254.bottom")}),-1.0]])]});
            var Q21;
            Q21=makeQuery(id+"F1.imprint","IMPRINT",FACE,{"disambiguationData":[TD([[makeQuery(id+"F1.imprint","IMPRINT",EDGE,{"derivedFrom":sQuery(id+"F1.wireOp",EDGE,"E99.top")}),-1.0]])]});
            var Q22;
            Q22=makeQuery(id+"F1.imprint","IMPRINT",FACE,{"disambiguationData":[TD([[makeQuery(id+"F1.imprint","IMPRINT",EDGE,{"derivedFrom":sQuery(id+"F1.wireOp",EDGE,"E256.MirrorCS")}),1.0]])]});
            var Q23;
            {var subQ0=sQuery(id+"F1.wireOp",EDGE,"E191.bottom");Q23=makeQuery(id+"F1.imprint","IMPRINT",FACE,{"disambiguationData":[TD([[makeQuery(id+"F1.imprint","IMPRINT",EDGE,{"derivedFrom":subQ0}),-1.0]])]});}
            var Q24;
            {var subQ0=sQuery(id+"F1.wireOp",EDGE,"E342.bottom");Q24=makeQuery(id+"F1.imprint","IMPRINT",FACE,{"disambiguationData":[TD([[makeQuery(id+"F1.imprint","IMPRINT",EDGE,{"derivedFrom":subQ0}),-1.0]])]});}
            var Q25;
            {var subQ3=sQuery(id+"F1.wireOp",EDGE,"E343.bottom");Q25=makeQuery(id+"F1.imprint","IMPRINT",FACE,{"disambiguationData":[TD([[makeQuery(id+"F1.imprint","IMPRINT",EDGE,{"derivedFrom":subQ3}),1.0]])]});}
            var Q26;
            {var subQ0=sQuery(id+"F1.wireOp",EDGE,"E151");Q26=makeQuery(id+"F1.imprint","IMPRINT",FACE,{"disambiguationData":[TD([[makeQuery(id+"F1.imprint","IMPRINT",EDGE,{"derivedFrom":subQ0}),1.0]])]});}
            var Q27;
            {var subQ1=sQuery(id+"F1.wireOp",EDGE,"E90");Q27=makeQuery(id+"F1.imprint","IMPRINT",FACE,{"disambiguationData":[TD([[makeQuery(id+"F1.imprint","IMPRINT",EDGE,{"derivedFrom":subQ1}),-1.0]])]});}
            var Q28;
            Q28=makeQuery(id+"F1.imprint","IMPRINT",FACE,{"disambiguationData":[TD([[makeQuery(id+"F1.imprint","IMPRINT",EDGE,{"derivedFrom":sQuery(id+"F1.wireOp",EDGE,"E94.bottom")}),1.0]])]});
            var Q29;
            Q29=makeQuery(id+"F1.imprint","IMPRINT",FACE,{"disambiguationData":[TD([[makeQuery(id+"F1.imprint","IMPRINT",EDGE,{"derivedFrom":sQuery(id+"F1.wireOp",EDGE,"E204.MirrorCS")}),1.0]])]});
            var Q30;
            Q30=makeQuery(id+"F1.imprint","IMPRINT",FACE,{"disambiguationData":[TD([[makeQuery(id+"F1.imprint","IMPRINT",EDGE,{"derivedFrom":sQuery(id+"F1.wireOp",EDGE,"E93.bottom")}),-1.0]])]});
            var Q31;
            Q31=makeQuery(id+"F1.imprint","IMPRINT",FACE,{"disambiguationData":[TD([[makeQuery(id+"F1.imprint","IMPRINT",EDGE,{"derivedFrom":sQuery(id+"F1.wireOp",EDGE,"E189.bottom")}),-1.0]])]});
            var Q32;
            {var subQ1=sQuery(id+"F1.wireOp",EDGE,"E179.MirrorCS");Q32=makeQuery(id+"F1.imprint","IMPRINT",FACE,{"disambiguationData":[TD([[makeQuery(id+"F1.imprint","IMPRINT",EDGE,{"derivedFrom":subQ1}),-1.0]])]});}
            var Q33;
            Q33=makeQuery(id+"F1.imprint","IMPRINT",FACE,{"disambiguationData":[TD([[makeQuery(id+"F1.imprint","IMPRINT",EDGE,{"derivedFrom":sQuery(id+"F1.wireOp",EDGE,"E174.MirrorCS")}),-1.0]])]});
            var Q34;
            Q34=makeQuery(id+"F1.imprint","IMPRINT",FACE,{"disambiguationData":[TD([[makeQuery(id+"F1.imprint","IMPRINT",EDGE,{"derivedFrom":sQuery(id+"F1.wireOp",EDGE,"E188.bottom")}),-1.0]])]});
            extrude(context, id + "F2", {"entities" : qUnion([Q0, Q1, Q2, Q3, Q4, Q5, Q6, Q7, Q8, Q9, Q10, Q11, Q12, Q13, Q14, Q15, Q16, Q17, Q18, Q19, Q20, Q21, Q22, Q23, Q24, Q25, Q26, Q27, Q28, Q29, Q30, Q31, Q32, Q33, Q34]), "depth" : (getVariable(context, 'ply34')) * mm});
        }
    });
